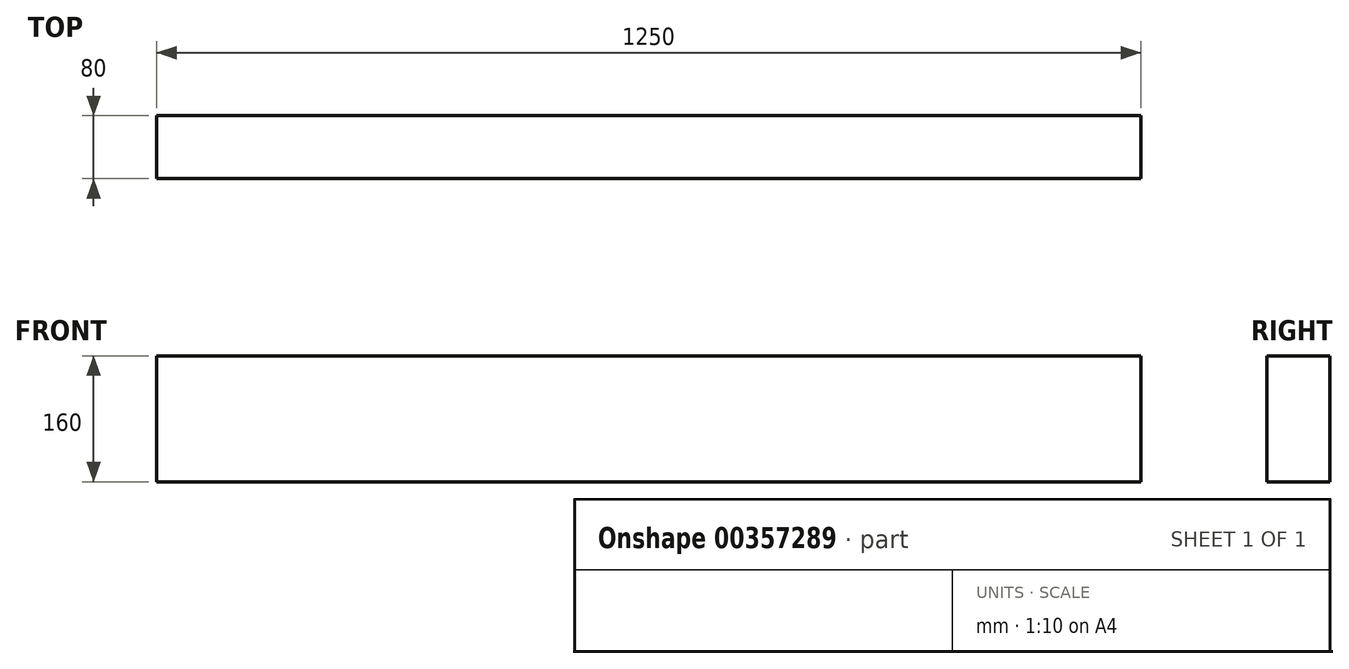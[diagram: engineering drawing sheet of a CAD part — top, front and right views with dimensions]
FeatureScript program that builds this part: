
annotation { "Feature Type Name" : "Feature", "Feature Type Description" : "" }
export const myFeature = defineFeature(function(context is Context, id is Id, definition is map)
    precondition{}
    {
        {
            var Q0;
            Q0=qCreatedBy(makeId("Right.planeOp"),FACE);
            var sketch = newSketch(context, id + "F0", { "sketchPlane" : qUnion([Q0])});
            skLineSegment(sketch, "E0.bottom", {"start": v(40, -80) * mm, "end": v(-40, -80) * mm});
            skLineSegment(sketch, "E0.top", {"start": v(40, 80) * mm, "end": v(-40, 80) * mm});
            skLineSegment(sketch, "E0.left", {"start": v(40, -80) * mm, "end": v(40, 80) * mm});
            skLineSegment(sketch, "E0.right", {"start": v(-40, -80) * mm, "end": v(-40, 80) * mm});
            skPoint(sketch, "E0.middle", {"position": v(0, 0) * mm});
            skSolve(sketch);
        }
        {
            var Q0;
            Q0 = qSketchRegion(id + "F0", true);
            extrude(context, id + "F1", {"entities" : qUnion([Q0]), "endBound" : BoundingType.SYMMETRIC, "oppositeDirection" : true, "depth" : 1250 * mm});
        }
    });
